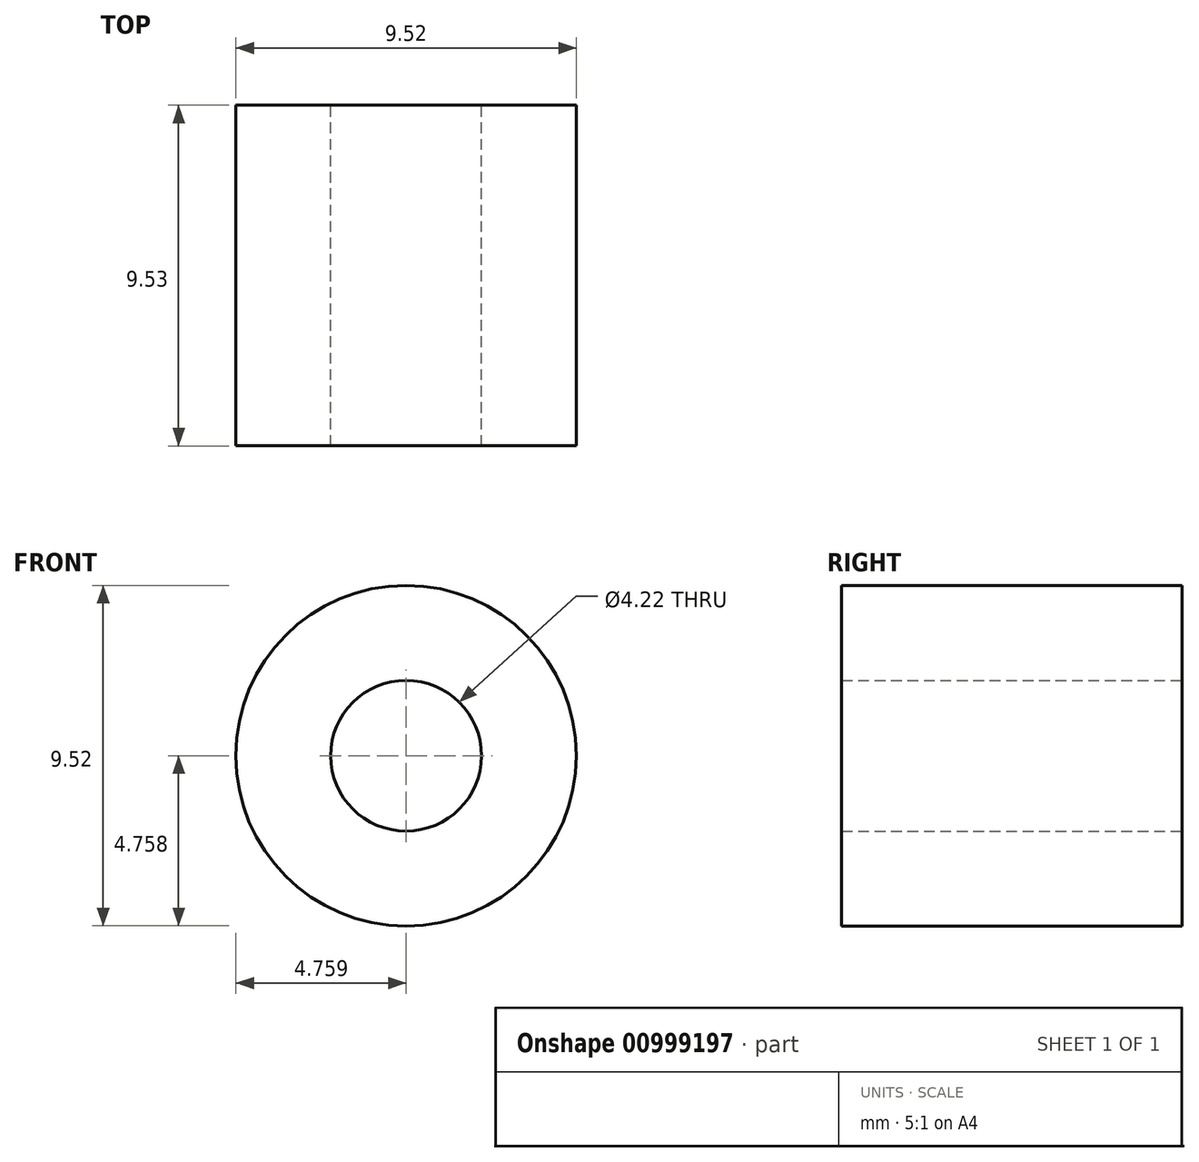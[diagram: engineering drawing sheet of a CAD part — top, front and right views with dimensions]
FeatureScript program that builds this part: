
annotation { "Feature Type Name" : "Feature", "Feature Type Description" : "" }
export const myFeature = defineFeature(function(context is Context, id is Id, definition is map)
    precondition{}
    {
        {
            var Q0;
            Q0=qCreatedBy(makeId("Front.planeOp"),FACE);
            var sketch = newSketch(context, id + "F0", { "sketchPlane" : qUnion([Q0])});
            skCircle(sketch, "E0", {"center": v(9.6, 16.86) * mm, "radius": 4.76 * mm});
            skCircle(sketch, "E1", {"center": v(9.6, 16.86) * mm, "radius": 2.1 * mm});
            skSolve(sketch);
        }
        {
            var Q0;
            Q0 = qSketchRegion(id + "F0", true);
            extrude(context, id + "F1", {"entities" : qUnion([Q0]), "depth" : 9.52 * mm, "offsetDistance" : 25.4 * mm});
        }
    });
